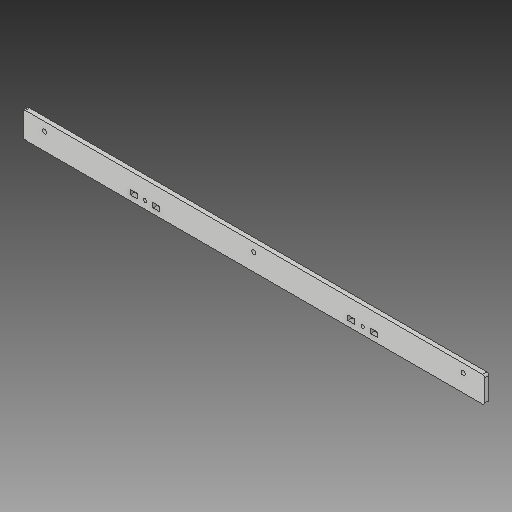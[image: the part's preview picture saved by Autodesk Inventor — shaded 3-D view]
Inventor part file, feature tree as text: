
AUTODESK INVENTOR PART (.ipt)
format: ipt  version: 2019 (Build 230136000, 136)  size: 158,208 bytes
history: native  units: mm
features: reference x12, extrude x2, sketch x2, other x2, fillet x1, helix x1
ambient origin geometry x8: Origin, YZ Plane, XZ Plane, XY Plane, X Axis, Y Axis, Z Axis, Center Point
bodies: Solid1 (feature_tree)
feature tree (20):
  extrude  "Extrusion1"  Depth=15.0mm
  fillet  "Fillet1"  Radius=0.2mm
  extrude  "Extrusion2"  Depth=4.0mm
  sketch  "Sketch1"  dims[d0=5.0mm d1=15.0mm d2=0.2mm]
  reference  "Reference1"
  reference  "Reference2"
  reference  "Reference3"
  reference  "Reference4"
  reference  "Reference5"
  reference  "Reference6"
  reference  "Reference7"
  reference  "Reference8"
  reference  "Reference9"
  reference  "Reference10"
  reference  "Reference11"
  reference  "Reference12"
  sketch  "Sketch2"  dims[d3=0.2mm d4=0.2mm d5=0.2mm d6=3.2mm d7=3.2mm d8=4.0mm d9=0.0mm d10=2.0mm d11=4.0mm d12=4.0mm d13=4.0mm d14=20.0mm d15=20.0mm d16=8.0mm d17=8.0mm d18=8.0mm d19=4.0mm d20=0.0mm]
  other  "<userpath>\Documents\CAD Files\Helix DLP\Helix DLP.iam"
  helix  "Helix DLP.iam"  [1 undecoded]
  other  "Wiper_Arm_1:1"
note: 1 required parameter value undecoded (feature->parameter linkage not recoverable at this tier; creation-order binding heuristic only, values carry confidence <= 0.55)
